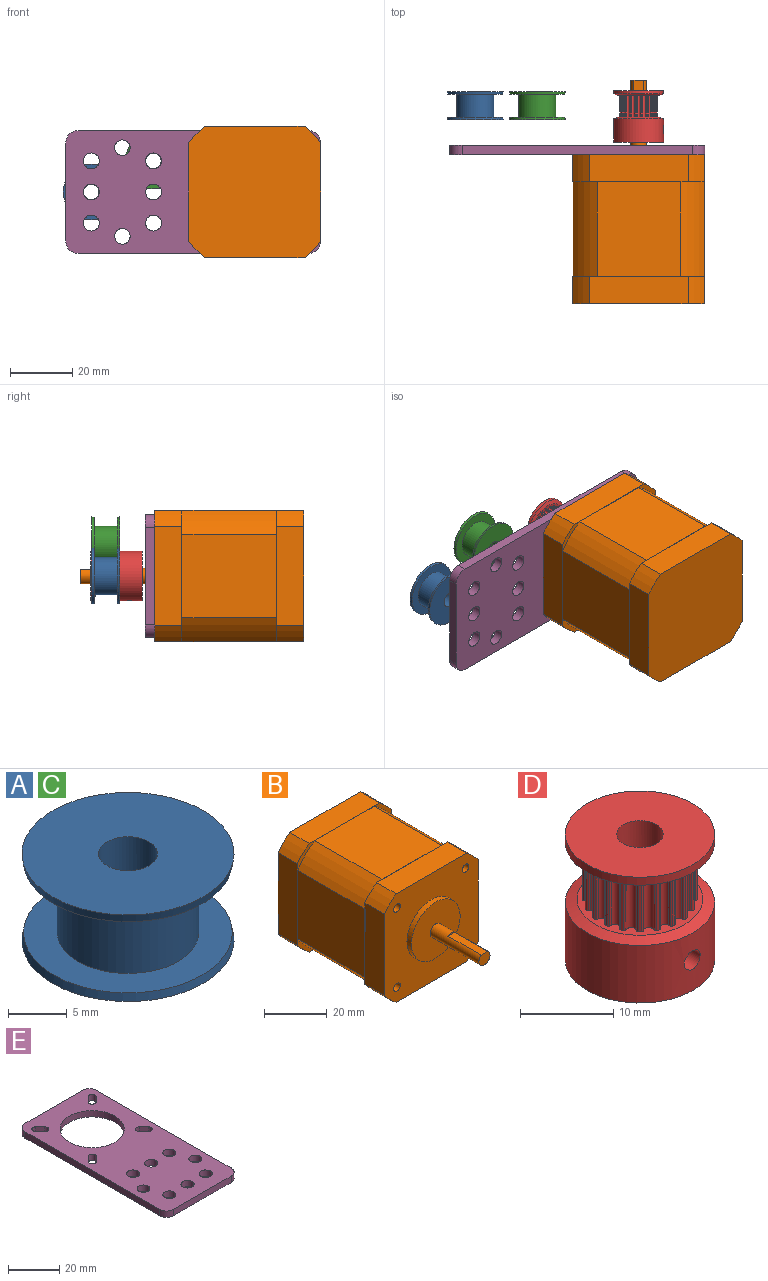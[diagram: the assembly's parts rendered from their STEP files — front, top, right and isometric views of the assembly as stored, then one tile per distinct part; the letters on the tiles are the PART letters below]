
ASSEMBLY  parts=5 mates=6
PART A: 8 faces, bbox 18x18x9 mm
  f0: plane 17.72x17.72mm, normal (0,0,-1), area 133.5mm2, adj f1,f6
  f1: cylinder r=6mm len=12mm, axis (0,0,-1), area 279mm2, adj f0,f2
  f2: plane 17.72x17.72mm, normal (0,0,1), area 133.5mm2, adj f1,f3
  f3: cone r=9mm half-angle=10deg, axis (0,0,-1), area 45.6mm2, adj f2,f4
  f4: plane 18x18mm, normal (0,0,-1), area 234.8mm2, adj f3,f7
  f5: plane 18x18mm, normal (0,0,1), area 234.8mm2, adj f6,f7
  f6: cone r=8.86mm half-angle=10deg, axis (0,0,1), area 45.6mm2, adj f0,f5
  f7: cylinder r=2.5mm len=9mm, axis (0,0,1), area 141.4mm2, adj f4,f5
PART B: 50 faces, bbox 42.4x72x42.4 mm
  f0: cylinder r=2.5mm len=22mm, axis (0,1,0), area 297.3mm2, adj f1,f2,f29,f30
  f1: plane 5x4.5mm, normal (0,-1,0), area 18.6mm2, adj f0,f29
  f2: plane 22x22mm, normal (0,-1,0), area 360.5mm2, adj f0,f3
  f3: cylinder r=11mm len=22mm, axis (0,1,0), area 138.2mm2, adj f2,f8
  f4: plane 31.78x8.75mm, normal (1,0,0), area 278mm2, adj f8,f9,f10,f32
  f5: plane 31.78x8.75mm, normal (0,0,-1), area 278mm2, adj f8,f9,f11,f32
  f6: plane 31.78x8.75mm, normal (-1,0,0), area 278mm2, adj f8,f11,f12,f32
  f7: plane 31.78x8.75mm, normal (0,0,1), area 278mm2, adj f8,f10,f12,f32
  f8: plane 42.42x42.42mm, normal (0,-1,0), area 1339.6mm2, adj f3,f4,f5,f6,f7,f9,f10,f11
  f9: cylinder r=26.5mm len=8.75mm, axis (0,1,0), area 66.1mm2, adj f4,f5,f8,f32
  f10: cylinder r=26.5mm len=8.75mm, axis (0,1,0), area 66.1mm2, adj f4,f7,f8,f32
  f11: cylinder r=26.5mm len=8.75mm, axis (0,1,0), area 66.1mm2, adj f5,f6,f8,f32
  f12: cylinder r=26.5mm len=8.75mm, axis (0,1,0), area 66.1mm2, adj f6,f7,f8,f32
  f13: cone r=1.25mm half-angle=59deg, axis (0,-1,0), area 5.7mm2, adj f14
  f14: cylinder r=1.25mm len=2.5mm, axis (0,-1,0), area 11.8mm2, adj f13,f15
  f15: plane 3x3mm, normal (0,-1,0), area 2.2mm2, adj f14,f16
  f16: cylinder r=1.5mm len=6mm, axis (0,-1,0), area 56.5mm2, adj f8,f15
  f17: cone r=1.25mm half-angle=59deg, axis (0,-1,0), area 5.7mm2, adj f18
  f18: cylinder r=1.25mm len=2.5mm, axis (0,-1,0), area 11.8mm2, adj f17,f19
  f19: plane 3x3mm, normal (0,-1,0), area 2.2mm2, adj f18,f20
  f20: cylinder r=1.5mm len=6mm, axis (0,-1,0), area 56.5mm2, adj f8,f19
  f21: cone r=1.25mm half-angle=59deg, axis (0,-1,0), area 5.7mm2, adj f22
  f22: cylinder r=1.25mm len=2.5mm, axis (0,-1,0), area 11.8mm2, adj f21,f23
  f23: plane 3x3mm, normal (0,-1,0), area 2.2mm2, adj f22,f24
  f24: cylinder r=1.5mm len=6mm, axis (0,-1,0), area 56.5mm2, adj f8,f23
  f25: cone r=1.25mm half-angle=59deg, axis (0,-1,0), area 5.7mm2, adj f26
  f26: cylinder r=1.25mm len=2.5mm, axis (0,-1,0), area 11.8mm2, adj f25,f27
  f27: plane 3x3mm, normal (0,-1,0), area 2.2mm2, adj f26,f28
  f28: cylinder r=1.5mm len=6mm, axis (0,-1,0), area 56.5mm2, adj f8,f27
  f29: plane 15x3mm, normal (0,0,1), area 45mm2, adj f0,f1,f30
  f30: plane 3x0.5mm, normal (0,-1,0), area 1mm2, adj f0,f29
  f31: plane 42.42x42.42mm, normal (0,-1,0), area 67.2mm2, adj f33,f34,f35,f36,f37,f38,f39,f40
  f32: plane 42.42x42.42mm, normal (0,1,0), area 67.2mm2, adj f4,f5,f6,f7,f9,f10,f11,f12
  f33: cylinder r=25mm len=30.5mm, axis (0,-1,0), area 335.5mm2, adj f31,f32,f34,f40
  f34: plane 30.5x26.79mm, normal (0,0,1), area 817.1mm2, adj f31,f32,f33,f35
  f35: cylinder r=25mm len=30.5mm, axis (0,-1,0), area 335.5mm2, adj f31,f32,f34,f36
  f36: plane 30.5x26.79mm, normal (1,0,0), area 817.1mm2, adj f31,f32,f35,f37
  f37: cylinder r=25mm len=30.5mm, axis (0,-1,0), area 335.5mm2, adj f31,f32,f36,f38
  f38: plane 30.5x26.79mm, normal (0,0,-1), area 817.1mm2, adj f31,f32,f37,f39
  f39: cylinder r=25mm len=30.5mm, axis (0,-1,0), area 335.5mm2, adj f31,f32,f38,f40
  f40: plane 30.5x26.79mm, normal (-1,0,0), area 817.1mm2, adj f31,f32,f33,f39
  f41: plane 42.42x42.42mm, normal (0,1,0), area 1748.1mm2, adj f42,f43,f44,f45,f46,f47,f48,f49
  f42: cylinder r=26.5mm len=8.75mm, axis (0,1,0), area 66.1mm2, adj f31,f41,f48,f49
  f43: cylinder r=26.5mm len=8.75mm, axis (0,1,0), area 66.1mm2, adj f31,f41,f47,f48
  f44: cylinder r=26.5mm len=8.75mm, axis (0,1,0), area 66.1mm2, adj f31,f41,f46,f47
  f45: cylinder r=26.5mm len=8.75mm, axis (0,1,0), area 66.1mm2, adj f31,f41,f46,f49
  f46: plane 31.78x8.75mm, normal (0,0,1), area 278mm2, adj f31,f41,f44,f45
  f47: plane 31.78x8.75mm, normal (-1,0,0), area 278mm2, adj f31,f41,f43,f44
  f48: plane 31.78x8.75mm, normal (0,0,-1), area 278mm2, adj f31,f41,f42,f43
  f49: plane 31.78x8.75mm, normal (1,0,0), area 278mm2, adj f31,f41,f42,f45
PART C: same geometry as A
PART D: 131 faces, bbox 16x16x16.5 mm
  f0: cylinder r=8mm len=16mm, axis (0,0,-1), area 370mm2, adj f123,f124,f129,f130
  f1: cylinder r=2.5mm len=16.5mm, axis (0,0,-1), area 249.8mm2, adj f123,f126,f129,f130
  f2: cylinder r=6.11mm len=7mm, axis (0,0,-1), area 2.2mm2, adj f3,f14,f122,f125
  f3: cylinder r=0.19mm len=7mm, axis (0,0,-1), area 1.8mm2, adj f2,f4,f122,f125
  f4: cylinder r=5mm len=7mm, axis (0,0,-1), area 1.6mm2, adj f3,f5,f122,f125
  f5: cylinder r=0.56mm len=7mm, axis (0,0,-1), area 9.4mm2, adj f4,f6,f122,f125
  f6: cylinder r=5mm len=7mm, axis (0,0,-1), area 1.6mm2, adj f5,f7,f122,f125
  f7: cylinder r=0.19mm len=7mm, axis (0,0,-1), area 1.8mm2, adj f6,f8,f122,f125
  f8: cylinder r=6.11mm len=7mm, axis (0,0,-1), area 2.2mm2, adj f7,f117,f122,f125
  f9: cylinder r=6.11mm len=7mm, axis (0,0,-1), area 2.2mm2, adj f10,f20,f122,f125
  f10: cylinder r=0.19mm len=7mm, axis (0,0,-1), area 1.8mm2, adj f9,f11,f122,f125
  f11: cylinder r=5mm len=7mm, axis (0,0,-1), area 1.6mm2, adj f10,f12,f122,f125
  f12: cylinder r=0.56mm len=7mm, axis (0,0,-1), area 9.4mm2, adj f11,f13,f122,f125
  f13: cylinder r=5mm len=7mm, axis (0,0,-1), area 1.6mm2, adj f12,f14,f122,f125
  f14: cylinder r=0.19mm len=7mm, axis (0,0,-1), area 1.8mm2, adj f2,f13,f122,f125
  f15: cylinder r=6.11mm len=7mm, axis (0,0,-1), area 2.2mm2, adj f16,f26,f122,f125
  f16: cylinder r=0.19mm len=7mm, axis (0,0,-1), area 1.8mm2, adj f15,f17,f122,f125
  f17: cylinder r=5mm len=7mm, axis (0,0,-1), area 1.6mm2, adj f16,f18,f122,f125
  f18: cylinder r=0.56mm len=7mm, axis (0,0,-1), area 9.4mm2, adj f17,f19,f122,f125
  f19: cylinder r=5mm len=7mm, axis (0,0,-1), area 1.6mm2, adj f18,f20,f122,f125
  f20: cylinder r=0.19mm len=7mm, axis (0,0,-1), area 1.8mm2, adj f9,f19,f122,f125
  f21: cylinder r=6.11mm len=7mm, axis (0,0,-1), area 2.2mm2, adj f22,f32,f122,f125
  f22: cylinder r=0.19mm len=7mm, axis (0,0,-1), area 1.8mm2, adj f21,f23,f122,f125
  f23: cylinder r=5mm len=7mm, axis (0,0,-1), area 1.6mm2, adj f22,f24,f122,f125
  f24: cylinder r=0.56mm len=7mm, axis (0,0,-1), area 9.4mm2, adj f23,f25,f122,f125
  f25: cylinder r=5mm len=7mm, axis (0,0,-1), area 1.6mm2, adj f24,f26,f122,f125
  f26: cylinder r=0.19mm len=7mm, axis (0,0,-1), area 1.8mm2, adj f15,f25,f122,f125
  f27: cylinder r=6.11mm len=7mm, axis (0,0,-1), area 2.2mm2, adj f28,f38,f122,f125
  f28: cylinder r=0.19mm len=7mm, axis (0,0,-1), area 1.8mm2, adj f27,f29,f122,f125
  f29: cylinder r=5mm len=7mm, axis (0,0,-1), area 1.6mm2, adj f28,f30,f122,f125
  f30: cylinder r=0.56mm len=7mm, axis (0,0,-1), area 9.4mm2, adj f29,f31,f122,f125
  f31: cylinder r=5mm len=7mm, axis (0,0,-1), area 1.6mm2, adj f30,f32,f122,f125
  f32: cylinder r=0.19mm len=7mm, axis (0,0,-1), area 1.8mm2, adj f21,f31,f122,f125
  f33: cylinder r=6.11mm len=7mm, axis (0,0,-1), area 2.2mm2, adj f34,f44,f122,f125
  f34: cylinder r=0.19mm len=7mm, axis (0,0,-1), area 1.8mm2, adj f33,f35,f122,f125
  f35: cylinder r=5mm len=7mm, axis (0,0,-1), area 1.6mm2, adj f34,f36,f122,f125
  f36: cylinder r=0.56mm len=7mm, axis (0,0,-1), area 9.4mm2, adj f35,f37,f122,f125
  f37: cylinder r=5mm len=7mm, axis (0,0,-1), area 1.6mm2, adj f36,f38,f122,f125
  f38: cylinder r=0.19mm len=7mm, axis (0,0,-1), area 1.8mm2, adj f27,f37,f122,f125
  f39: cylinder r=6.11mm len=7mm, axis (0,0,-1), area 2.2mm2, adj f40,f50,f122,f125
  f40: cylinder r=0.19mm len=7mm, axis (0,0,-1), area 1.8mm2, adj f39,f41,f122,f125
  f41: cylinder r=5mm len=7mm, axis (0,0,-1), area 1.6mm2, adj f40,f42,f122,f125
  f42: cylinder r=0.56mm len=7mm, axis (0,0,-1), area 9.4mm2, adj f41,f43,f122,f125
  f43: cylinder r=5mm len=7mm, axis (0,0,-1), area 1.6mm2, adj f42,f44,f122,f125
  f44: cylinder r=0.19mm len=7mm, axis (0,0,-1), area 1.8mm2, adj f33,f43,f122,f125
  f45: cylinder r=6.11mm len=7mm, axis (0,0,-1), area 2.2mm2, adj f46,f56,f122,f125
  f46: cylinder r=0.19mm len=7mm, axis (0,0,-1), area 1.8mm2, adj f45,f47,f122,f125
  f47: cylinder r=5mm len=7mm, axis (0,0,-1), area 1.6mm2, adj f46,f48,f122,f125
  f48: cylinder r=0.56mm len=7mm, axis (0,0,-1), area 9.4mm2, adj f47,f49,f122,f125
  f49: cylinder r=5mm len=7mm, axis (0,0,-1), area 1.6mm2, adj f48,f50,f122,f125
  f50: cylinder r=0.19mm len=7mm, axis (0,0,-1), area 1.8mm2, adj f39,f49,f122,f125
  f51: cylinder r=6.11mm len=7mm, axis (0,0,-1), area 2.2mm2, adj f52,f62,f122,f125
  f52: cylinder r=0.19mm len=7mm, axis (0,0,-1), area 1.8mm2, adj f51,f53,f122,f125
  f53: cylinder r=5mm len=7mm, axis (0,0,-1), area 1.6mm2, adj f52,f54,f122,f125
  f54: cylinder r=0.56mm len=7mm, axis (0,0,-1), area 9.4mm2, adj f53,f55,f122,f125
  f55: cylinder r=5mm len=7mm, axis (0,0,-1), area 1.6mm2, adj f54,f56,f122,f125
  f56: cylinder r=0.19mm len=7mm, axis (0,0,-1), area 1.8mm2, adj f45,f55,f122,f125
  f57: cylinder r=6.11mm len=7mm, axis (0,0,-1), area 2.2mm2, adj f58,f68,f122,f125
  f58: cylinder r=0.19mm len=7mm, axis (0,0,-1), area 1.8mm2, adj f57,f59,f122,f125
  f59: cylinder r=5mm len=7mm, axis (0,0,-1), area 1.6mm2, adj f58,f60,f122,f125
  f60: cylinder r=0.56mm len=7mm, axis (0,0,-1), area 9.4mm2, adj f59,f61,f122,f125
  f61: cylinder r=5mm len=7mm, axis (0,0,-1), area 1.6mm2, adj f60,f62,f122,f125
  f62: cylinder r=0.19mm len=7mm, axis (0,0,-1), area 1.8mm2, adj f51,f61,f122,f125
  f63: cylinder r=6.11mm len=7mm, axis (0,0,-1), area 2.2mm2, adj f64,f74,f122,f125
  f64: cylinder r=0.19mm len=7mm, axis (0,0,-1), area 1.8mm2, adj f63,f65,f122,f125
  f65: cylinder r=5mm len=7mm, axis (0,0,-1), area 1.6mm2, adj f64,f66,f122,f125
  f66: cylinder r=0.56mm len=7mm, axis (0,0,-1), area 9.4mm2, adj f65,f67,f122,f125
  f67: cylinder r=5mm len=7mm, axis (0,0,-1), area 1.6mm2, adj f66,f68,f122,f125
  f68: cylinder r=0.19mm len=7mm, axis (0,0,-1), area 1.8mm2, adj f57,f67,f122,f125
  f69: cylinder r=6.11mm len=7mm, axis (0,0,-1), area 2.2mm2, adj f70,f80,f122,f125
  f70: cylinder r=0.19mm len=7mm, axis (0,0,-1), area 1.8mm2, adj f69,f71,f122,f125
  f71: cylinder r=5mm len=7mm, axis (0,0,-1), area 1.6mm2, adj f70,f72,f122,f125
  f72: cylinder r=0.56mm len=7mm, axis (0,0,-1), area 9.4mm2, adj f71,f73,f122,f125
  f73: cylinder r=5mm len=7mm, axis (0,0,-1), area 1.6mm2, adj f72,f74,f122,f125
  f74: cylinder r=0.19mm len=7mm, axis (0,0,-1), area 1.8mm2, adj f63,f73,f122,f125
  f75: cylinder r=6.11mm len=7mm, axis (0,0,-1), area 2.2mm2, adj f76,f86,f122,f125
  f76: cylinder r=0.19mm len=7mm, axis (0,0,-1), area 1.8mm2, adj f75,f77,f122,f125
  f77: cylinder r=5mm len=7mm, axis (0,0,-1), area 1.6mm2, adj f76,f78,f122,f125
  f78: cylinder r=0.56mm len=7mm, axis (0,0,-1), area 9.4mm2, adj f77,f79,f122,f125
  f79: cylinder r=5mm len=7mm, axis (0,0,-1), area 1.6mm2, adj f78,f80,f122,f125
  f80: cylinder r=0.19mm len=7mm, axis (0,0,-1), area 1.8mm2, adj f69,f79,f122,f125
  f81: cylinder r=6.11mm len=7mm, axis (0,0,-1), area 2.2mm2, adj f82,f92,f122,f125
  f82: cylinder r=0.19mm len=7mm, axis (0,0,-1), area 1.8mm2, adj f81,f83,f122,f125
  f83: cylinder r=5mm len=7mm, axis (0,0,-1), area 1.6mm2, adj f82,f84,f122,f125
  f84: cylinder r=0.56mm len=7mm, axis (0,0,-1), area 9.4mm2, adj f83,f85,f122,f125
  f85: cylinder r=5mm len=7mm, axis (0,0,-1), area 1.6mm2, adj f84,f86,f122,f125
  f86: cylinder r=0.19mm len=7mm, axis (0,0,-1), area 1.8mm2, adj f75,f85,f122,f125
  f87: cylinder r=6.11mm len=7mm, axis (0,0,-1), area 2.2mm2, adj f88,f98,f122,f125
  f88: cylinder r=0.19mm len=7mm, axis (0,0,-1), area 1.8mm2, adj f87,f89,f122,f125
  f89: cylinder r=5mm len=7mm, axis (0,0,-1), area 1.6mm2, adj f88,f90,f122,f125
  f90: cylinder r=0.56mm len=7mm, axis (0,0,-1), area 9.4mm2, adj f89,f91,f122,f125
  f91: cylinder r=5mm len=7mm, axis (0,0,-1), area 1.6mm2, adj f90,f92,f122,f125
  f92: cylinder r=0.19mm len=7mm, axis (0,0,-1), area 1.8mm2, adj f81,f91,f122,f125
  f93: cylinder r=6.11mm len=7mm, axis (0,0,-1), area 2.2mm2, adj f94,f104,f122,f125
  f94: cylinder r=0.19mm len=7mm, axis (0,0,-1), area 1.8mm2, adj f93,f95,f122,f125
  f95: cylinder r=5mm len=7mm, axis (0,0,-1), area 1.6mm2, adj f94,f96,f122,f125
  f96: cylinder r=0.56mm len=7mm, axis (0,0,-1), area 9.4mm2, adj f95,f97,f122,f125
  f97: cylinder r=5mm len=7mm, axis (0,0,-1), area 1.6mm2, adj f96,f98,f122,f125
  f98: cylinder r=0.19mm len=7mm, axis (0,0,-1), area 1.8mm2, adj f87,f97,f122,f125
  f99: cylinder r=6.11mm len=7mm, axis (0,0,-1), area 2.2mm2, adj f100,f110,f122,f125
  f100: cylinder r=0.19mm len=7mm, axis (0,0,-1), area 1.8mm2, adj f99,f101,f122,f125
  f101: cylinder r=5mm len=7mm, axis (0,0,-1), area 1.6mm2, adj f100,f102,f122,f125
  f102: cylinder r=0.56mm len=7mm, axis (0,0,-1), area 9.4mm2, adj f101,f103,f122,f125
  f103: cylinder r=5mm len=7mm, axis (0,0,-1), area 1.6mm2, adj f102,f104,f122,f125
  f104: cylinder r=0.19mm len=7mm, axis (0,0,-1), area 1.8mm2, adj f93,f103,f122,f125
  f105: cylinder r=6.11mm len=7mm, axis (0,0,-1), area 2.2mm2, adj f106,f116,f122,f125
  f106: cylinder r=0.19mm len=7mm, axis (0,0,-1), area 1.8mm2, adj f105,f107,f122,f125
  f107: cylinder r=5mm len=7mm, axis (0,0,-1), area 1.6mm2, adj f106,f108,f122,f125
  f108: cylinder r=0.56mm len=7mm, axis (0,0,-1), area 9.4mm2, adj f107,f109,f122,f125
  f109: cylinder r=5mm len=7mm, axis (0,0,-1), area 1.6mm2, adj f108,f110,f122,f125
  f110: cylinder r=0.19mm len=7mm, axis (0,0,-1), area 1.8mm2, adj f99,f109,f122,f125
  f111: cylinder r=6.11mm len=7mm, axis (0,0,-1), area 2.2mm2, adj f112,f121,f122,f125
  f112: cylinder r=0.19mm len=7mm, axis (0,0,-1), area 1.8mm2, adj f111,f113,f122,f125
  f113: cylinder r=5mm len=7mm, axis (0,0,-1), area 1.6mm2, adj f112,f114,f122,f125
  f114: cylinder r=0.56mm len=7mm, axis (0,0,-1), area 9.4mm2, adj f113,f115,f122,f125
  f115: cylinder r=5mm len=7mm, axis (0,0,-1), area 1.6mm2, adj f114,f116,f122,f125
  f116: cylinder r=0.19mm len=7mm, axis (0,0,-1), area 1.8mm2, adj f105,f115,f122,f125
  f117: cylinder r=0.19mm len=7mm, axis (0,0,-1), area 1.8mm2, adj f8,f118,f122,f125
  f118: cylinder r=5mm len=7mm, axis (0,0,-1), area 1.6mm2, adj f117,f119,f122,f125
  f119: cylinder r=0.56mm len=7mm, axis (0,0,-1), area 9.4mm2, adj f118,f120,f122,f125
  f120: cylinder r=5mm len=7mm, axis (0,0,-1), area 1.6mm2, adj f119,f121,f122,f125
  f121: cylinder r=0.19mm len=7mm, axis (0,0,-1), area 1.8mm2, adj f111,f120,f122,f125
  f122: plane 13.48x13.48mm, normal (0,0,1), area 40mm2, adj f2,f3,f4,f5,f6,f7,f8,f9
  f123: plane 16x16mm, normal (0,0,-1), area 181.4mm2, adj f0,f1
  f124: cone r=6.74mm half-angle=70deg, axis (0,0,-1), area 62mm2, adj f0,f122
  f125: plane 13.48x13.48mm, normal (0,0,-1), area 40mm2, adj f2,f3,f4,f5,f6,f7,f8,f9
  f126: plane 16x16mm, normal (0,0,1), area 181.4mm2, adj f1,f128
  f127: cone r=8mm half-angle=70deg, axis (0,0,1), area 62mm2, adj f125,f128
  f128: cylinder r=8mm len=16mm, axis (0,0,-1), area 52.4mm2, adj f126,f127
  f129: cylinder r=1.2mm len=5.81mm, axis (0,1,0), area 42.3mm2, adj f0,f1
  f130: cylinder r=1.2mm len=5.81mm, axis (-1,0,0), area 42.3mm2, adj f0,f1
PART E: 35 faces, bbox 39.5x82x3 mm
  f0: plane 82x39.5mm, normal (0,0,1), area 2498.5mm2, adj f2,f3,f4,f5,f6,f7,f8,f9
  f1: plane 82x39.5mm, normal (0,0,-1), area 2498.5mm2, adj f2,f3,f4,f5,f6,f7,f8,f9
  f2: cylinder r=4mm len=4mm, axis (0,0,-1), area 18.8mm2, adj f0,f1,f3,f9
  f3: plane 31.5x3mm, normal (0,-1,0), area 94.5mm2, adj f0,f1,f2,f4
  f4: cylinder r=4mm len=4mm, axis (0,0,-1), area 18.8mm2, adj f0,f1,f3,f5
  f5: plane 74x3mm, normal (1,0,0), area 222mm2, adj f0,f1,f4,f6
  f6: cylinder r=4mm len=4mm, axis (0,0,-1), area 18.8mm2, adj f0,f1,f5,f7
  f7: plane 31.5x3mm, normal (0,1,0), area 94.5mm2, adj f0,f1,f6,f8
  f8: cylinder r=4mm len=4mm, axis (0,0,-1), area 18.8mm2, adj f0,f1,f7,f9
  f9: plane 74x3mm, normal (-1,0,0), area 222mm2, adj f0,f1,f2,f8
  f10: cylinder r=12.5mm len=25mm, axis (0,0,-1), area 235.6mm2, adj f0,f1
  f11: cylinder r=1.55mm len=3mm, axis (0,0,-1), area 14.6mm2, adj f0,f1,f12,f14
  f12: plane 3x2.5mm, normal (-0.71,0.71,0), area 10.6mm2, adj f0,f1,f11,f13
  f13: cylinder r=1.55mm len=3mm, axis (0,0,-1), area 14.6mm2, adj f0,f1,f12,f14
  f14: plane 3x2.5mm, normal (0.71,-0.71,0), area 10.6mm2, adj f0,f1,f11,f13
  f15: cylinder r=2.55mm len=5.1mm, axis (0,0,-1), area 48.1mm2, adj f0,f1
  f16: cylinder r=2.55mm len=5.1mm, axis (0,0,-1), area 48.1mm2, adj f0,f1
  f17: cylinder r=2.55mm len=5.1mm, axis (0,0,-1), area 48.1mm2, adj f0,f1
  f18: cylinder r=2.55mm len=5.1mm, axis (0,0,-1), area 48.1mm2, adj f0,f1
  f19: cylinder r=2.55mm len=5.1mm, axis (0,0,-1), area 48.1mm2, adj f0,f1
  f20: cylinder r=2.55mm len=5.1mm, axis (0,0,-1), area 48.1mm2, adj f0,f1
  f21: cylinder r=1.55mm len=3mm, axis (0,0,-1), area 14.6mm2, adj f0,f1,f22,f24
  f22: plane 3x2.5mm, normal (-0.71,-0.71,0), area 10.6mm2, adj f0,f1,f21,f23
  f23: cylinder r=1.55mm len=3mm, axis (0,0,-1), area 14.6mm2, adj f0,f1,f22,f24
  f24: plane 3x2.5mm, normal (0.71,0.71,0), area 10.6mm2, adj f0,f1,f21,f23
  f25: cylinder r=1.55mm len=3mm, axis (0,0,-1), area 14.6mm2, adj f0,f1,f26,f28
  f26: plane 3x2.5mm, normal (0.71,-0.71,0), area 10.6mm2, adj f0,f1,f25,f27
  f27: cylinder r=1.55mm len=3mm, axis (0,0,-1), area 14.6mm2, adj f0,f1,f26,f28
  f28: plane 3x2.5mm, normal (-0.71,0.71,0), area 10.6mm2, adj f0,f1,f25,f27
  f29: cylinder r=1.55mm len=3mm, axis (0,0,-1), area 14.6mm2, adj f0,f1,f30,f32
  f30: plane 3x2.5mm, normal (0.71,0.71,0), area 10.6mm2, adj f0,f1,f29,f31
  f31: cylinder r=1.55mm len=3mm, axis (0,0,-1), area 14.6mm2, adj f0,f1,f30,f32
  f32: plane 3x2.5mm, normal (-0.71,-0.71,0), area 10.6mm2, adj f0,f1,f29,f31
  f33: cylinder r=2.5mm len=5mm, axis (0,0,1), area 47.1mm2, adj f0,f1
  f34: cylinder r=2.5mm len=5mm, axis (0,0,1), area 47.1mm2, adj f0,f1
PLACE A rot(axis=(1,0,0),90deg) t=(1540.15,-906.06,62.25)mm
PLACE B rot(axis=(0,0,-1),180deg) t=(1592.7,-929,62.25)mm
PLACE C rot(axis=(1,0,0),90deg) t=(1560.15,-906.06,72.25)mm
PLACE D rot(axis=(-0.58,0.58,0.58),120deg) t=(1592.7,-913.45,62.25)mm
PLACE E rot(axis=(0.58,0.58,-0.58),120deg) t=(1592.7,-926,62.25)mm
MATE planar D.f78 <-> C.f1  axis (0,1,0) through (1597.49,-916.95,65.73)mm
MATE slider C.f1 <-> E.f20  axis (0,-1,0) through (1560.15,-917.75,72.25)mm
MATE planar C.f1 <-> A.f1  axis (0,1,0) through (1560.15,-916.95,72.25)mm
MATE slider D.f0 <-> B.f0  axis (0,1,0) through (1592.7,-908.45,62.25)mm
MATE fastened B.f0 <-> E.f10  axis (0,1,0) through (1592.7,-929,62.25)mm
MATE slider A.f1 <-> E.f17  axis (0,-1,0) through (1540.15,-917.75,62.25)mm
